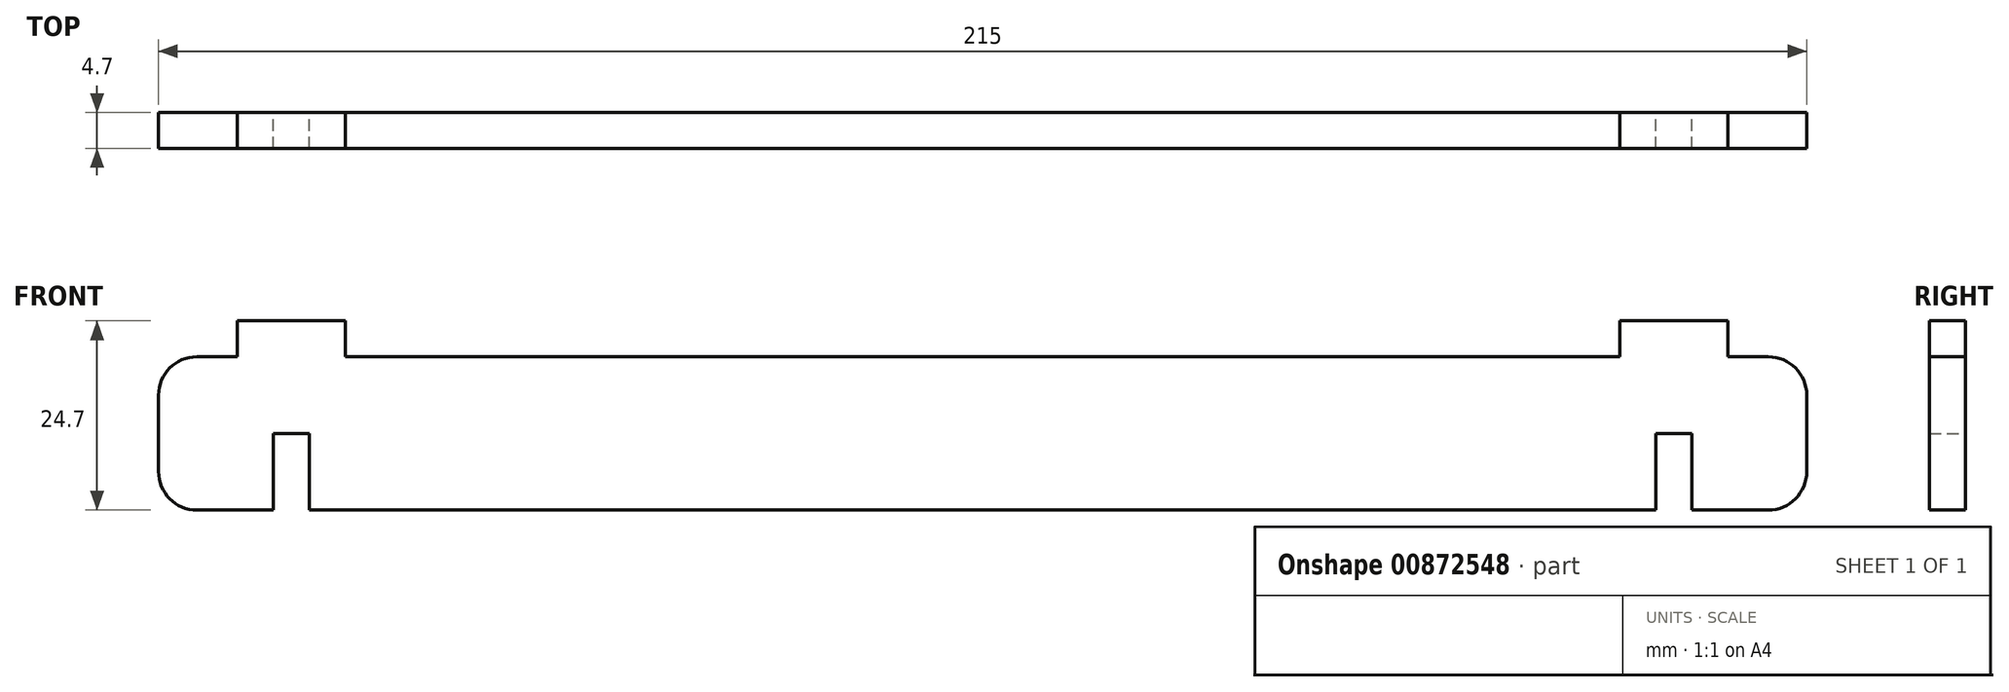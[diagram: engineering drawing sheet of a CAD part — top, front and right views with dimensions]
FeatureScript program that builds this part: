
annotation { "Feature Type Name" : "Feature", "Feature Type Description" : "" }
export const myFeature = defineFeature(function(context is Context, id is Id, definition is map)
    precondition{}
    {
        {
            assignVariable(context, id + "F0", {"name" : "e", "anyValue" : 4.7});
        }
        {
            var Q0;
            Q0=qCreatedBy(makeId("Front.planeOp"),FACE);
            var sketch = newSketch(context, id + "F1", { "sketchPlane" : qUnion([Q0])});
            skLineSegment(sketch, "E0.bottom", {"start": v(-102.5, 20) * mm, "end": v(-97.2, 20) * mm});
            skLineSegment(sketch, "E0.top", {"start": v(-102.5, 0) * mm, "end": v(-92.5, 0) * mm});
            skLineSegment(sketch, "E0.left", {"start": v(-107.5, 15) * mm, "end": v(-107.5, 5) * mm});
            skLineSegment(sketch, "E0.right", {"start": v(107.5, 15) * mm, "end": v(107.5, 5) * mm});
            skPoint(sketch, "E1", {"position": v(0, 0) * mm});
            skPoint(sketch, "E2.visualSharp", {"position": v(-107.5, 20) * mm});
            skArc(sketch, "E2.filletArc", {"start": v(-102.5, 20) * mm, "mid": v(-106.04, 18.54) * mm, "end": v(-107.5, 15) * mm});
            skPoint(sketch, "E3.visualSharp", {"position": v(107.5, 20) * mm});
            skArc(sketch, "E3.filletArc", {"start": v(107.5, 15) * mm, "mid": v(106.04, 18.54) * mm, "end": v(102.5, 20) * mm});
            skPoint(sketch, "E4.visualSharp", {"position": v(107.5, 0) * mm});
            skArc(sketch, "E4.filletArc", {"start": v(102.5, 0) * mm, "mid": v(106.04, 1.46) * mm, "end": v(107.5, 5) * mm});
            skPoint(sketch, "E5.visualSharp", {"position": v(-107.5, 0) * mm});
            skArc(sketch, "E5.filletArc", {"start": v(-107.5, 5) * mm, "mid": v(-106.04, 1.46) * mm, "end": v(-102.5, 0) * mm});
            skLineSegment(sketch, "E6", {"start": v(-92.5, 0) * mm, "end": v(-92.5, 10) * mm});
            skLineSegment(sketch, "E7", {"start": v(-92.5, 10) * mm, "end": v(-87.8, 10) * mm});
            skLineSegment(sketch, "E8", {"start": v(-87.8, 10) * mm, "end": v(-87.8, 0) * mm});
            skLineSegment(sketch, "E9.trimOffspring", {"start": v(-87.8, 0) * mm, "end": v(87.8, 0) * mm});
            skLineSegment(sketch, "E10", {"start": v(87.8, 0) * mm, "end": v(87.8, 10) * mm});
            skLineSegment(sketch, "E11", {"start": v(87.8, 10) * mm, "end": v(92.5, 10) * mm});
            skLineSegment(sketch, "E12", {"start": v(92.5, 10) * mm, "end": v(92.5, 0) * mm});
            skLineSegment(sketch, "E13.trimOffspring", {"start": v(92.5, 0) * mm, "end": v(102.5, 0) * mm});
            skLineSegment(sketch, "E14", {"start": v(-83.1, 20) * mm, "end": v(83.1, 20) * mm});
            skLineSegment(sketch, "E15", {"start": v(-97.2, 20) * mm, "end": v(-97.2, 24.7) * mm});
            skLineSegment(sketch, "E16", {"start": v(-97.2, 24.7) * mm, "end": v(-92.5, 24.7) * mm});
            skLineSegment(sketch, "E17", {"start": v(-83.1, 24.7) * mm, "end": v(-83.1, 20) * mm});
            skLineSegment(sketch, "E18", {"start": v(-92.5, 10) * mm, "end": v(-92.5, 24.7) * mm, "construction": true});
            skLineSegment(sketch, "E19", {"start": v(-87.8, 10) * mm, "end": v(-87.8, 24.7) * mm, "construction": true});
            skLineSegment(sketch, "E20", {"start": v(-92.5, 24.7) * mm, "end": v(-92.5, 24.7) * mm});
            skLineSegment(sketch, "E21", {"start": v(-87.8, 24.7) * mm, "end": v(-83.1, 24.7) * mm});
            skLineSegment(sketch, "E22", {"start": v(-92.5, 24.7) * mm, "end": v(-87.8, 24.7) * mm});
            skLineSegment(sketch, "E23", {"start": v(87.8, 10) * mm, "end": v(87.8, 24.7) * mm, "construction": true});
            skLineSegment(sketch, "E24", {"start": v(92.5, 10) * mm, "end": v(92.5, 24.7) * mm, "construction": true});
            skLineSegment(sketch, "E25", {"start": v(97.2, 20) * mm, "end": v(102.5, 20) * mm});
            skLineSegment(sketch, "E26", {"start": v(83.1, 20) * mm, "end": v(83.1, 24.7) * mm});
            skLineSegment(sketch, "E27", {"start": v(83.1, 24.7) * mm, "end": v(87.8, 24.7) * mm});
            skLineSegment(sketch, "E28", {"start": v(97.2, 24.7) * mm, "end": v(97.2, 20) * mm});
            skLineSegment(sketch, "E29", {"start": v(87.8, 24.7) * mm, "end": v(92.5, 24.7) * mm});
            skLineSegment(sketch, "E30", {"start": v(92.5, 24.7) * mm, "end": v(97.2, 24.7) * mm});
            skSolve(sketch);
        }
        {
            var Q0;
            Q0 = qSketchRegion(id + "F1", true);
            extrude(context, id + "F2", {"entities" : qUnion([Q0]), "depth" : (getVariable(context, 'e')) * mm, "offsetDistance" : 25 * mm});
        }
    });
